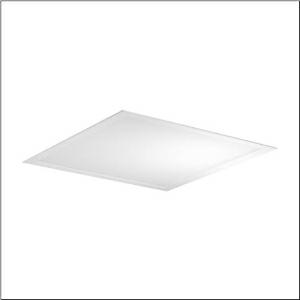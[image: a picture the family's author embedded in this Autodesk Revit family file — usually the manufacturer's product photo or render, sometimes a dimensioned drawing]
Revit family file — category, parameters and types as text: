
# Revit family: apollon_r__31_square_51mp11wd2m42_c9df
name_source: partatom
category: Lighting Fixtures
units: mm (PartAtom-declared; Revit-internal decimal feet)

## family parameters
Cut with Voids When Loaded = No
Host = Face
Light Source = No
Part Type = Normal
Room Calculation Point = No
Round Connector Dimension = Use Diameter
Shared = No

## types (1)
- --- (1 x LED, 4000 lm, 27.5 W, 4000K)
    Apparent Load = 28 VA
    CIE Flux Codes = 62 87 97 100 100
    Color Rendering = 80
    Color Temperature = 4000K
    Default Elevation = 1800 mm
    Description = Apollon® 31 square, office luminaire, primary optical cover: micro prismatic cover, of PMMA, CAT 2 (L<= 3000cd/m²), light emission: direct distribution, primary light characteristic: symmetric, installation type: lay-in mounting, LED, rated luminous flux: 4.000lm, luminous efficacy: 145lm/W, light colour: 830/840, colour temperature: 3000/4000K, control gear: DALI 2, Multilumen, with terminal, 5-pole, mains connection: 220..240V, AC/DC, 0/50..60Hz, rated input power: 28W, housing, of aluminium, traffic white (RAL 9016), module: M625, length: 620mm, width: 620mm, height: 62mm, recess depth: 180mm, housing upper side, of sheet steel, coated, protection rating (complete): IP20, protection rating (on room side): IP40, insulation class (complete): insulation class II (safety insulation), certification: CE, ENEC, impact resistance: IK03, permissible operating ambient temperature: -20..+40°C, permissible storage temperature: -20..+60°C, standard: EN 60598-2-22, packaging unit: 1 piece
    Height = 0 mm  [stored 0 ft]
    Lamp = 1 x LED
    Lamp Light Flux = 4000 lm
    Lamp Power = 27.5 W
    Lamp count = 1
    Length = 620 mm
    Luminous efficacy = 145 lm/W
    Manufacturer = Siteco
    ModVariant = No
    Model = 51MP11WD2M42
    Mounting Place = Ceiling
    Mounting Type = Recessed
    Number of Poles = 1
    OnlyDefault = Yes
    Power Factor = 1
    Product Name = Apollon® 31 square
    Product group = office luminaire | ceiling recessed
    ProductGroupID = 401
    Protection Class = Protection class II
    Protection Degree = IP 20
    RLX_Detail_Level = 1
    RLX_Emergency_Light_Flux = 0 lm
    RLX_Emergency_Type = 0
    RLX_Emergency_Type_DB = No
    RlxData = <blob elided: 13257 chars, md5=f3753fd4>
    Socket = socket
    Standby Power = 0 W
    System Light Flux = 4000 lm
    System Power = 28 W
    Type Comments = factory setting: colour temperature 4000K
    Type Image = l_1291039.jpg
    URL = http://relux.com
    VarID = @adj_076636
    Voltage = 0 V
    Weight = 0.00 kg
    Width = 620 mm

note: [stored X ft] marks values corroborated as IEEE doubles in the binary element streams (Revit-internal decimal feet)

## geometry (parser evidence)
native form markers: Sweep x11
no freeform markers — native parametric forms only
